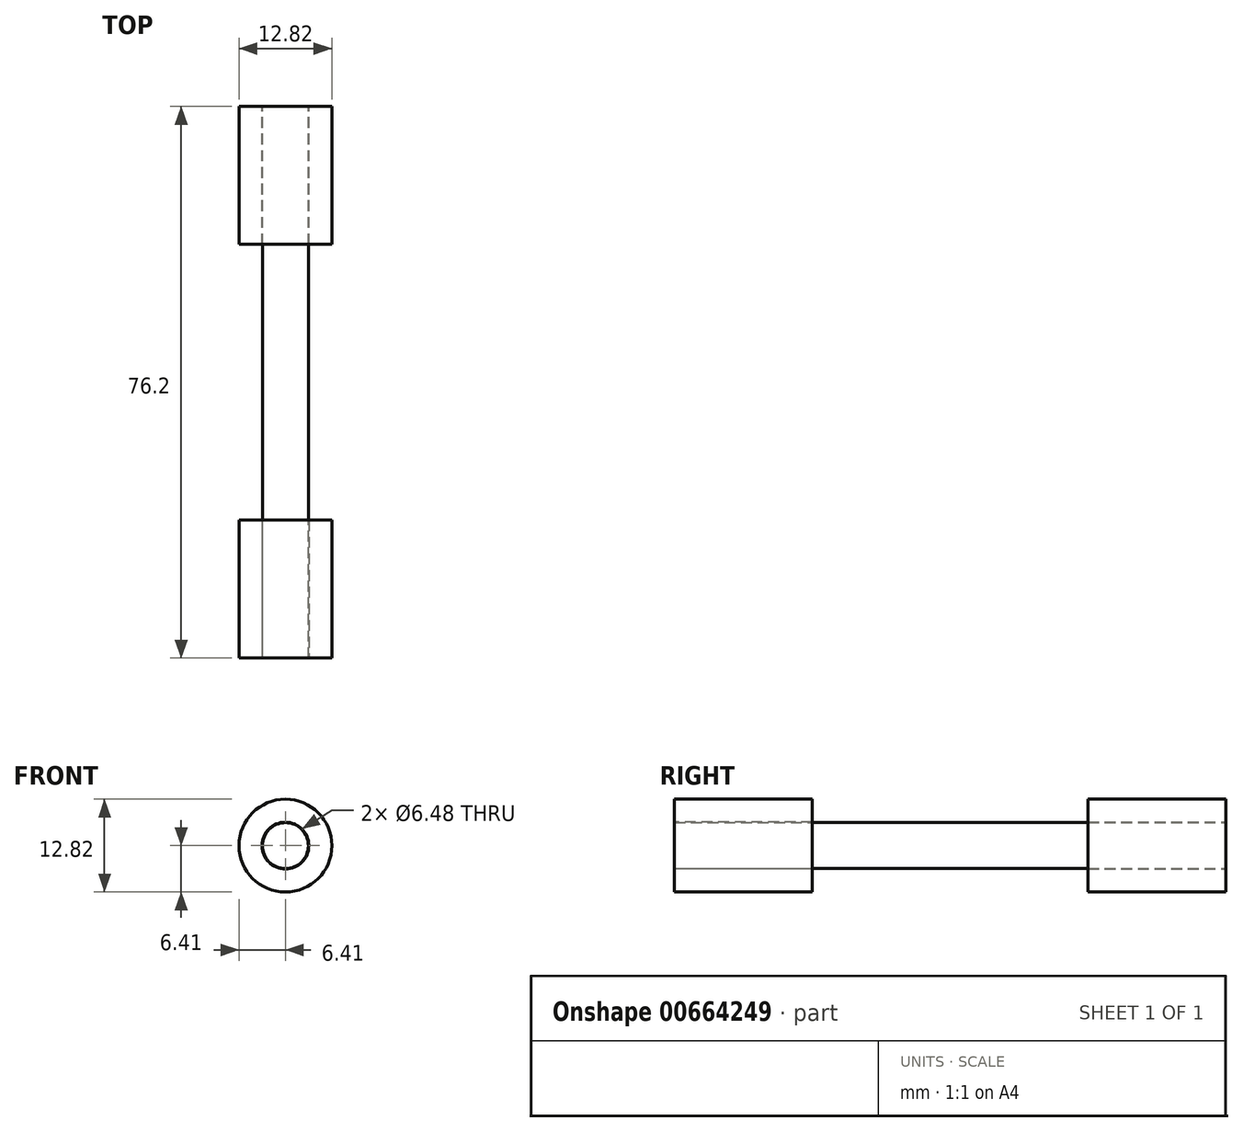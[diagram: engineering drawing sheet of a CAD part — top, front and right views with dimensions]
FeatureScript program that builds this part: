
annotation { "Feature Type Name" : "Feature", "Feature Type Description" : "" }
export const myFeature = defineFeature(function(context is Context, id is Id, definition is map)
    precondition{}
    {
        {
            var Q0;
            Q0=qCreatedBy(makeId("Front.planeOp"),FACE);
            var sketch = newSketch(context, id + "F0", { "sketchPlane" : qUnion([Q0])});
            skCircle(sketch, "E0", {"center": v(0, 0) * mm, "radius": 3.18 * mm});
            skSolve(sketch);
        }
        {
            var Q0;
            Q0 = qSketchRegion(id + "F0", true);
            extrude(context, id + "F1", {"entities" : qUnion([Q0]), "depth" : 76.2 * mm, "offsetDistance" : 25.4 * mm, "symmetric" : true});
        }
        {
            var Q0;
            Q0=makeQuery(id+"F1.opExtrude","CAP_FACE",FACE,{"disambiguationData":[OSD([sQuery(id+"F0.wireOp",EDGE,"E0")])],"isStart":false});
            var sketch = newSketch(context, id + "F2", { "sketchPlane" : qUnion([Q0])});
            skCircle(sketch, "E1", {"center": v(0, 0) * mm, "radius": 3.24 * mm});
            skCircle(sketch, "E2", {"center": v(0, 0) * mm, "radius": 6.41 * mm});
            skSolve(sketch);
        }
        {
            var Q0;
            Q0 = qSketchRegion(id + "F2", true);
            extrude(context, id + "F3", {"entities" : qUnion([Q0]), "oppositeDirection" : true, "depth" : 19.05 * mm, "offsetDistance" : 25.4 * mm});
        }
        {
            var Q0;
            Q0=makeQuery(id+"F1.opExtrude","CAP_FACE",FACE,{"disambiguationData":[OSD([sQuery(id+"F0.wireOp",EDGE,"E0")])],"isStart":true});
            var sketch = newSketch(context, id + "F4", { "sketchPlane" : qUnion([Q0])});
            skCircle(sketch, "E3", {"center": v(0, 0) * mm, "radius": 3.24 * mm});
            skCircle(sketch, "E4", {"center": v(0, 0) * mm, "radius": 6.41 * mm});
            skSolve(sketch);
        }
        {
            var Q0;
            Q0 = qSketchRegion(id + "F4", true);
            extrude(context, id + "F5", {"entities" : qUnion([Q0]), "oppositeDirection" : true, "depth" : 19.05 * mm, "offsetDistance" : 25.4 * mm});
        }
    });
